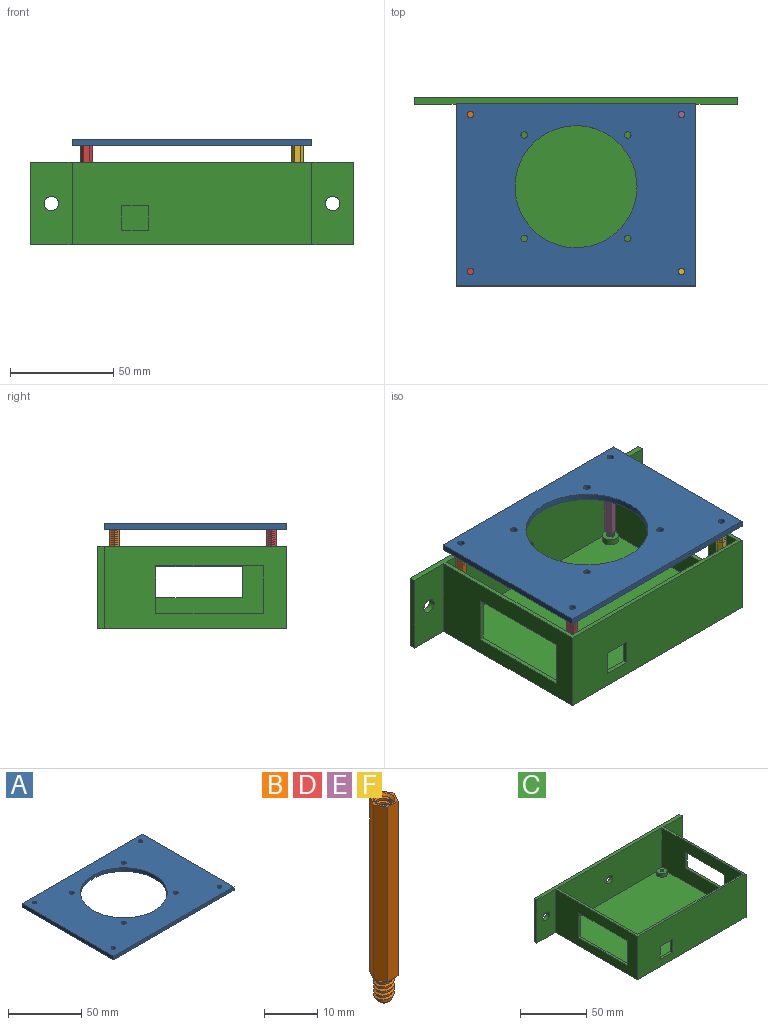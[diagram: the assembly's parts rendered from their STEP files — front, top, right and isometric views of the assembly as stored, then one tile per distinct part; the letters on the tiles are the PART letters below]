
ASSEMBLY  parts=6 mates=3
PART A: 15 faces, bbox 116x88x3 mm
  f0: plane 88x3mm, normal (-1,0,0), area 264mm2, adj f1,f3,f4,f5
  f1: plane 116x3mm, normal (0,-1,0), area 348mm2, adj f0,f2,f4,f5
  f2: plane 88x3mm, normal (1,0,0), area 264mm2, adj f1,f3,f4,f5
  f3: plane 116x3mm, normal (0,1,0), area 348mm2, adj f0,f2,f4,f5
  f4: plane 116x88mm, normal (0,0,1), area 7409.7mm2, adj f0,f1,f2,f3,f6,f7,f8,f9
  f5: plane 116x88mm, normal (0,0,-1), area 7409.7mm2, adj f0,f1,f2,f3,f6,f7,f8,f9
  f6: cylinder r=1.6mm len=3.2mm, axis (0,0,1), area 30.2mm2, adj f4,f5
  f7: cylinder r=1.6mm len=3.2mm, axis (0,0,1), area 30.2mm2, adj f4,f5
  f8: cylinder r=1.6mm len=3.2mm, axis (0,0,1), area 30.2mm2, adj f4,f5
  f9: cylinder r=1.6mm len=3.2mm, axis (0,0,1), area 30.2mm2, adj f4,f5
  f10: cylinder r=1.6mm len=3.2mm, axis (0,0,1), area 30.2mm2, adj f4,f5
  f11: cylinder r=1.6mm len=3.2mm, axis (0,0,1), area 30.2mm2, adj f4,f5
  f12: cylinder r=1.6mm len=3.2mm, axis (0,0,1), area 30.2mm2, adj f4,f5
  f13: cylinder r=1.6mm len=3.2mm, axis (0,0,1), area 30.2mm2, adj f4,f5
  f14: cylinder r=29.5mm len=59mm, axis (0,0,1), area 556.1mm2, adj f4,f5
PART B: 20 faces, bbox 5.6x4.9x46.5 mm
  f0: cylinder r=1.5mm len=9.5mm, axis (0,0,1), area 55.3mm2, adj f9,f16,f17,f18,f19
  f1: plane 40x2.35mm, normal (0.87,-0.5,0), area 108.5mm2, adj f2,f6,f7,f8
  f2: plane 40x2.35mm, normal (0.87,0.5,0), area 108.5mm2, adj f1,f3,f7,f8
  f3: plane 40x2.71mm, normal (0,1,0), area 108.5mm2, adj f2,f4,f7,f8
  f4: plane 40x2.35mm, normal (-0.87,0.5,0), area 108.5mm2, adj f3,f5,f7,f8
  f5: plane 40x2.35mm, normal (-0.87,-0.5,0), area 108.5mm2, adj f4,f6,f7,f8
  f6: plane 40x2.71mm, normal (0,-1,0), area 108.5mm2, adj f1,f5,f7,f8
  f7: plane 5.43x4.7mm, normal (0,0,1), area 6.6mm2, adj f1,f2,f3,f4,f5,f6,f16
  f8: plane 5.59x4.86mm, normal (0,0,-1), area 10.9mm2, adj f1,f2,f3,f4,f5,f6,f10,f13
  f9: plane 3x3mm, normal (0,0,1), area 7.1mm2, adj f0
  f10: cylinder r=1.5mm len=5.5mm, axis (0,0,1), area 27.7mm2, adj f8,f12,f13,f14,f15
  f11: plane 2x2mm, normal (0,0,-1), area 3.1mm2, adj f12
  f12: cone r=1mm half-angle=45deg, axis (0,0,1), area 5.6mm2, adj f10,f11
  f13: bspline ~5.58x4.46mm, area 27.8mm2, adj f8,f10,f14,f15
  f14: bspline ~5.75x4.46mm, area 29mm2, adj f8,f10,f13,f15
  f15: plane 0.5x0.43mm, normal (0,-1,0), area 0.1mm2, adj f10,f13,f14
  f16: cone r=1.5mm half-angle=45deg, axis (0,0,1), area 6.2mm2, adj f0,f7,f18,f19
  f17: plane 0.5x0.43mm, normal (0,1,0), area 0.1mm2, adj f0,f18,f19
  f18: bspline ~10.08x4.46mm, area 51.7mm2, adj f0,f16,f17,f19
  f19: bspline ~10.08x4.46mm, area 50.8mm2, adj f0,f16,f17,f18
PART C: 42 faces, bbox 156x91x40 mm
  f0: plane 88x40mm, normal (-1,0,0), area 2324mm2, adj f2,f4,f5,f30,f35,f36,f37,f38
  f1: plane 86x38mm, normal (1,0,0), area 2072mm2, adj f2,f7,f8,f9,f35,f36,f37,f38
  f2: plane 156x91mm, normal (0,0,1), area 1044mm2, adj f0,f1,f3,f4,f6,f7,f8,f30
  f3: plane 88x40mm, normal (1,0,0), area 2890mm2, adj f2,f4,f5,f26,f27,f28,f29,f31
  f4: plane 116x40mm, normal (0,-1,0), area 4484mm2, adj f0,f2,f3,f5,f22,f23,f24,f25
  f5: plane 156x91mm, normal (0,0,-1), area 10649.6mm2, adj f0,f3,f4,f18,f19,f20,f21,f30
  f6: plane 86x38mm, normal (-1,0,0), area 2638mm2, adj f2,f7,f8,f9,f26,f27,f28,f29
  f7: plane 112x38mm, normal (0,-1,0), area 4217.5mm2, adj f1,f2,f6,f9,f40
  f8: plane 112x38mm, normal (0,1,0), area 4100mm2, adj f1,f2,f6,f9,f22,f23,f24,f25
  f9: plane 112x86mm, normal (0,0,1), area 9430.9mm2, adj f1,f6,f7,f8,f10,f12,f14,f16
  f10: cylinder r=4mm len=8mm, axis (0,0,-1), area 75.4mm2, adj f9,f11
  f11: plane 8x8mm, normal (0,0,1), area 43.7mm2, adj f10,f21
  f12: cylinder r=4mm len=8mm, axis (0,0,-1), area 75.4mm2, adj f9,f13
  f13: plane 8x8mm, normal (0,0,1), area 43.7mm2, adj f12,f20
  f14: cylinder r=4mm len=8mm, axis (0,0,-1), area 75.4mm2, adj f9,f15
  f15: plane 8x8mm, normal (0,0,1), area 43.7mm2, adj f14,f19
  f16: cylinder r=4mm len=8mm, axis (0,0,-1), area 75.4mm2, adj f9,f17
  f17: plane 8x8mm, normal (0,0,1), area 43.7mm2, adj f16,f18
  f18: cylinder r=1.45mm len=5mm, axis (0,0,1), area 45.6mm2, adj f5,f17
  f19: cylinder r=1.45mm len=5mm, axis (0,0,1), area 45.6mm2, adj f5,f15
  f20: cylinder r=1.45mm len=5mm, axis (0,0,1), area 45.6mm2, adj f5,f13
  f21: cylinder r=1.45mm len=5mm, axis (0,0,1), area 45.6mm2, adj f5,f11
  f22: plane 12x2mm, normal (1,0,0), area 24mm2, adj f4,f8,f23,f24
  f23: plane 13x2mm, normal (0,0,-1), area 26mm2, adj f4,f8,f22,f25
  f24: plane 13x2mm, normal (0,0,1), area 26mm2, adj f4,f8,f22,f25
  f25: plane 12x2mm, normal (-1,0,0), area 24mm2, adj f4,f8,f23,f24
  f26: plane 15x2mm, normal (0,1,0), area 30mm2, adj f3,f6,f27,f28
  f27: plane 42x2mm, normal (0,0,-1), area 84mm2, adj f3,f6,f26,f29
  f28: plane 42x2mm, normal (0,0,1), area 84mm2, adj f3,f6,f26,f29
  f29: plane 15x2mm, normal (0,-1,0), area 30mm2, adj f3,f6,f27,f28
  f30: plane 40x20mm, normal (0,-1,0), area 761.5mm2, adj f0,f2,f5,f34,f41
  f31: plane 40x20mm, normal (0,-1,0), area 761.5mm2, adj f2,f3,f5,f32,f39
  f32: plane 40x3mm, normal (1,0,0), area 120mm2, adj f2,f5,f31,f33
  f33: plane 156x40mm, normal (0,1,0), area 6124.5mm2, adj f2,f5,f32,f34,f39,f40,f41
  f34: plane 40x3mm, normal (-1,0,0), area 120mm2, adj f2,f5,f30,f33
  f35: plane 52x2mm, normal (0,0,1), area 104mm2, adj f0,f1,f36,f38
  f36: plane 23x2mm, normal (0,1,0), area 46mm2, adj f0,f1,f35,f37
  f37: plane 52x2mm, normal (0,0,-1), area 104mm2, adj f0,f1,f36,f38
  f38: plane 23x2mm, normal (0,-1,0), area 46mm2, adj f0,f1,f35,f37
  f39: cylinder r=3.5mm len=7mm, axis (0,-1,0), area 66mm2, adj f31,f33
  f40: cylinder r=3.5mm len=7mm, axis (0,-1,0), area 66mm2, adj f7,f33
  f41: cylinder r=3.5mm len=7mm, axis (0,-1,0), area 66mm2, adj f30,f33
PART D: same geometry as B
PART E: same geometry as B
PART F: same geometry as B
PLACE A t=(0,0,1.2)mm
PLACE B t=(-51,38,8)mm
PLACE C at identity
PLACE D t=(-51,-38,8.2)mm
PLACE E t=(51,38,8)mm
PLACE F t=(51,-38,9.2)mm
MATE fastened E.f10 <-> C.f14  axis (0,0,-1) through (51,38,2)mm
MATE fastened B.f10 <-> C.f12  axis (0,0,-1) through (-51,38,2)mm
MATE fastened A.f6 <-> D.f0  axis (0,0,-1) through (-51,-38,48.2)mm
